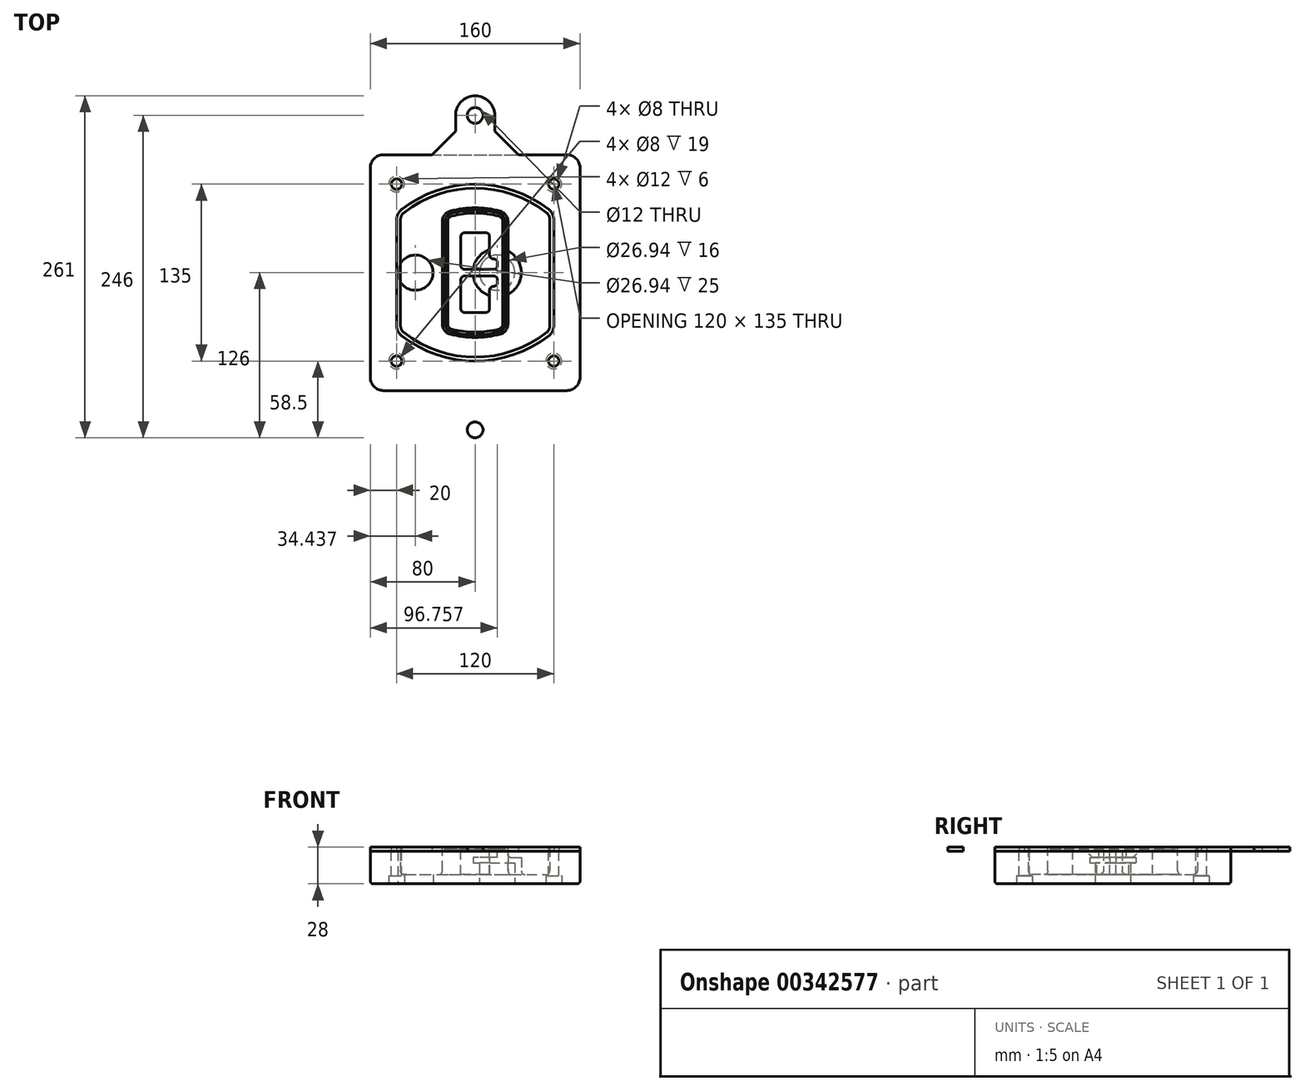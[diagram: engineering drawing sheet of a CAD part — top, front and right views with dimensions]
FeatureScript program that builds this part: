
annotation { "Feature Type Name" : "Feature", "Feature Type Description" : "" }
export const myFeature = defineFeature(function(context is Context, id is Id, definition is map)
    precondition{}
    {
        {
            var Q0;
            Q0=qCreatedBy(makeId("Top.planeOp"),FACE);
            var sketch = newSketch(context, id + "F0", { "sketchPlane" : qUnion([Q0])});
            skPoint(sketch, "E0.rect.middle", {"position": v(0, 0) * mm});
            skLineSegment(sketch, "E1.bottom", {"start": v(-70, -90) * mm, "end": v(70, -90) * mm});
            skLineSegment(sketch, "E1.top", {"start": v(-70, 90) * mm, "end": v(70, 90) * mm});
            skLineSegment(sketch, "E1.left", {"start": v(-80, -80) * mm, "end": v(-80, 80) * mm});
            skLineSegment(sketch, "E1.right", {"start": v(80, -80) * mm, "end": v(80, 80) * mm});
            skLineSegment(sketch, "E2", {"start": v(-80, 90) * mm, "end": v(80, -90) * mm, "construction": true});
            skLineSegment(sketch, "E3", {"start": v(80, 90) * mm, "end": v(-80, -90) * mm, "construction": true});
            skCircle(sketch, "E4", {"center": v(-60, 67.5) * mm, "radius": 4 * mm});
            skCircle(sketch, "E5", {"center": v(60, 67.5) * mm, "radius": 4 * mm});
            skCircle(sketch, "E6", {"center": v(60, -67.5) * mm, "radius": 4 * mm});
            skCircle(sketch, "E7", {"center": v(-60, -67.5) * mm, "radius": 4 * mm});
            skLineSegment(sketch, "E8", {"start": v(-60, 67.5) * mm, "end": v(60, 67.5) * mm, "construction": true});
            skLineSegment(sketch, "E9", {"start": v(60, 67.5) * mm, "end": v(60, -67.5) * mm, "construction": true});
            skLineSegment(sketch, "E10", {"start": v(60, -67.5) * mm, "end": v(-60, -67.5) * mm, "construction": true});
            skLineSegment(sketch, "E11", {"start": v(-60, -67.5) * mm, "end": v(-60, 67.5) * mm, "construction": true});
            skLineSegment(sketch, "E12", {"start": v(-60, 40.3) * mm, "end": v(-60, -40.3) * mm});
            skLineSegment(sketch, "E13", {"start": v(60, 40.3) * mm, "end": v(60, -40.3) * mm});
            skArc(sketch, "E14", {"start": v(56.15, 48.18) * mm, "mid": v(0, 67.5) * mm, "end": v(-56.15, 48.18) * mm});
            skArc(sketch, "E15", {"start": v(-56.15, -48.18) * mm, "mid": v(0, -67.5) * mm, "end": v(56.15, -48.18) * mm});
            skLineSegment(sketch, "E16", {"start": v(-60, 0) * mm, "end": v(60, 0) * mm, "construction": true});
            skPoint(sketch, "E17.visualSharp", {"position": v(-60, -45) * mm});
            skArc(sketch, "E17.filletArc", {"start": v(-60, -40.3) * mm, "mid": v(-58.99, -44.68) * mm, "end": v(-56.15, -48.18) * mm});
            skPoint(sketch, "E18.visualSharp", {"position": v(-60, 45) * mm});
            skArc(sketch, "E18.filletArc", {"start": v(-56.15, 48.18) * mm, "mid": v(-58.99, 44.68) * mm, "end": v(-60, 40.3) * mm});
            skPoint(sketch, "E19.visualSharp", {"position": v(60, 45) * mm});
            skArc(sketch, "E19.filletArc", {"start": v(60, 40.3) * mm, "mid": v(58.99, 44.68) * mm, "end": v(56.15, 48.18) * mm});
            skPoint(sketch, "E20.visualSharp", {"position": v(60, -45) * mm});
            skArc(sketch, "E20.filletArc", {"start": v(56.15, -48.18) * mm, "mid": v(58.99, -44.68) * mm, "end": v(60, -40.3) * mm});
            skPoint(sketch, "E21.visualSharp", {"position": v(-80, 90) * mm});
            skArc(sketch, "E21.filletArc", {"start": v(-70, 90) * mm, "mid": v(-77.07, 87.07) * mm, "end": v(-80, 80) * mm});
            skPoint(sketch, "E22.visualSharp", {"position": v(80, 90) * mm});
            skArc(sketch, "E22.filletArc", {"start": v(80, 80) * mm, "mid": v(77.07, 87.07) * mm, "end": v(70, 90) * mm});
            skPoint(sketch, "E23.visualSharp", {"position": v(80, -90) * mm});
            skArc(sketch, "E23.filletArc", {"start": v(70, -90) * mm, "mid": v(77.07, -87.07) * mm, "end": v(80, -80) * mm});
            skPoint(sketch, "E24.visualSharp", {"position": v(-80, -90) * mm});
            skArc(sketch, "E24.filletArc", {"start": v(-80, -80) * mm, "mid": v(-77.07, -87.07) * mm, "end": v(-70, -90) * mm});
            skArc(sketch, "E25.0", {"start": v(57, 40.3) * mm, "mid": v(56.3, 43.36) * mm, "end": v(54.3, 45.81) * mm});
            skLineSegment(sketch, "E25.1", {"start": v(57, 40.3) * mm, "end": v(57, -40.3) * mm});
            skArc(sketch, "E25.2", {"start": v(54.3, -45.81) * mm, "mid": v(56.3, -43.36) * mm, "end": v(57, -40.3) * mm});
            skArc(sketch, "E25.3", {"start": v(-54.3, -45.81) * mm, "mid": v(0, -64.5) * mm, "end": v(54.3, -45.81) * mm});
            skArc(sketch, "E25.4", {"start": v(-57, -40.3) * mm, "mid": v(-56.3, -43.36) * mm, "end": v(-54.3, -45.81) * mm});
            skArc(sketch, "E25.5", {"start": v(54.3, 45.81) * mm, "mid": v(0, 64.5) * mm, "end": v(-54.3, 45.81) * mm});
            skLineSegment(sketch, "E25.6", {"start": v(-57, 40.3) * mm, "end": v(-57, -40.3) * mm});
            skArc(sketch, "E25.7", {"start": v(-54.3, 45.81) * mm, "mid": v(-56.3, 43.36) * mm, "end": v(-57, 40.3) * mm});
            skArc(sketch, "E26.0", {"start": v(-58.62, 51.33) * mm, "mid": v(-62.58, 46.43) * mm, "end": v(-64, 40.3) * mm});
            skArc(sketch, "E26.1", {"start": v(58.62, 51.33) * mm, "mid": v(0, 71.5) * mm, "end": v(-58.62, 51.33) * mm});
            skArc(sketch, "E26.2", {"start": v(64, 40.3) * mm, "mid": v(62.58, 46.43) * mm, "end": v(58.62, 51.33) * mm});
            skLineSegment(sketch, "E26.3", {"start": v(64, 40.3) * mm, "end": v(64, -40.3) * mm});
            skArc(sketch, "E26.4", {"start": v(58.62, -51.33) * mm, "mid": v(62.58, -46.43) * mm, "end": v(64, -40.3) * mm});
            skLineSegment(sketch, "E26.5", {"start": v(-64, 40.3) * mm, "end": v(-64, -40.3) * mm});
            skArc(sketch, "E26.6", {"start": v(-58.62, -51.33) * mm, "mid": v(0, -71.5) * mm, "end": v(58.62, -51.33) * mm});
            skArc(sketch, "E26.7", {"start": v(-64, -40.3) * mm, "mid": v(-62.58, -46.43) * mm, "end": v(-58.62, -51.33) * mm});
            skSolve(sketch);
        }
        {
            var Q0;
            Q0=makeQuery(id+"F0.imprint","IMPRINT",FACE,{"disambiguationData":[TD([[makeQuery(id+"F0.imprint","IMPRINT",EDGE,{"derivedFrom":sQuery(id+"F0.wireOp",EDGE,"E1.bottom")}),1.0]])]});
            var Q1;
            Q1=makeQuery(id+"F0.imprint","IMPRINT",FACE,{"disambiguationData":[TD([[makeQuery(id+"F0.imprint","IMPRINT",EDGE,{"derivedFrom":sQuery(id+"F0.wireOp",EDGE,"E12")}),1.0]])]});
            var Q2;
            Q2=makeQuery(id+"F0.imprint","IMPRINT",FACE,{"disambiguationData":[TD([[makeQuery(id+"F0.imprint","IMPRINT",EDGE,{"derivedFrom":sQuery(id+"F0.wireOp",EDGE,"E25.0")}),1.0]])]});
            var Q3;
            Q3=makeQuery(id+"F0.imprint","IMPRINT",FACE,{"disambiguationData":[TD([[makeQuery(id+"F0.imprint","IMPRINT",EDGE,{"derivedFrom":sQuery(id+"F0.wireOp",EDGE,"E12")}),-1.0]])]});
            extrude(context, id + "F1", {"entities" : qUnion([Q0, Q1, Q2, Q3]), "oppositeDirection" : true, "depth" : 25 * mm});
        }
        {
            var Q0;
            Q0=makeQuery(id+"F0.imprint","IMPRINT",FACE,{"disambiguationData":[TD([[makeQuery(id+"F0.imprint","IMPRINT",EDGE,{"derivedFrom":sQuery(id+"F0.wireOp",EDGE,"E12")}),1.0]])]});
            extrude(context, id + "F2", {"entities" : qUnion([Q0]), "operationType" : NewBodyOperationType.ADD, "depth" : 3 * mm});
        }
        {
            var Q0;
            Q0=makeQuery(id+"F0.imprint","IMPRINT",FACE,{"disambiguationData":[TD([[makeQuery(id+"F0.imprint","IMPRINT",EDGE,{"derivedFrom":sQuery(id+"F0.wireOp",EDGE,"E25.0")}),1.0]])]});
            extrude(context, id + "F3", {"entities" : qUnion([Q0]), "operationType" : NewBodyOperationType.REMOVE, "oppositeDirection" : true, "depth" : 18 * mm});
        }
        {
            var Q0;
            Q0=makeQuery(id+"F2.opExtrude","CAP_FACE",FACE,{"disambiguationData":[OSD([sQuery(id+"F0.wireOp",EDGE,"E12"),sQuery(id+"F0.wireOp",EDGE,"E13"),sQuery(id+"F0.wireOp",EDGE,"E14"),sQuery(id+"F0.wireOp",EDGE,"E15"),sQuery(id+"F0.wireOp",EDGE,"E17.filletArc"),sQuery(id+"F0.wireOp",EDGE,"E18.filletArc"),sQuery(id+"F0.wireOp",EDGE,"E19.filletArc"),sQuery(id+"F0.wireOp",EDGE,"E20.filletArc"),sQuery(id+"F0.wireOp",EDGE,"E25.0"),sQuery(id+"F0.wireOp",EDGE,"E25.1"),sQuery(id+"F0.wireOp",EDGE,"E25.2"),sQuery(id+"F0.wireOp",EDGE,"E25.3"),sQuery(id+"F0.wireOp",EDGE,"E25.4"),sQuery(id+"F0.wireOp",EDGE,"E25.5"),sQuery(id+"F0.wireOp",EDGE,"E25.6"),sQuery(id+"F0.wireOp",EDGE,"E25.7")])],"isStart":false});
            var sketch = newSketch(context, id + "F4", { "sketchPlane" : qUnion([Q0])});
            skArc(sketch, "E27.0", {"start": v(-19.08, -46.97) * mm, "mid": v(0, -49.5) * mm, "end": v(19.08, -46.97) * mm});
            skArc(sketch, "E28.0", {"start": v(19.08, 46.97) * mm, "mid": v(0, 49.5) * mm, "end": v(-19.08, 46.97) * mm});
            skLineSegment(sketch, "E29", {"start": v(-25, 39.25) * mm, "end": v(-25, -39.25) * mm});
            skLineSegment(sketch, "E30", {"start": v(25, 39.25) * mm, "end": v(25, -39.25) * mm});
            skLineSegment(sketch, "E31", {"start": v(-25, 45.1) * mm, "end": v(25, 45.1) * mm, "construction": true});
            skLineSegment(sketch, "E32", {"start": v(-25, -45.1) * mm, "end": v(25, -45.1) * mm, "construction": true});
            skPoint(sketch, "E33.visualSharp", {"position": v(-25, 45.1) * mm});
            skArc(sketch, "E33.filletArc", {"start": v(-19.08, 46.97) * mm, "mid": v(-23.35, 44.11) * mm, "end": v(-25, 39.25) * mm});
            skPoint(sketch, "E34.visualSharp", {"position": v(25, 45.1) * mm});
            skArc(sketch, "E34.filletArc", {"start": v(25, 39.25) * mm, "mid": v(23.35, 44.11) * mm, "end": v(19.08, 46.97) * mm});
            skPoint(sketch, "E35.visualSharp", {"position": v(25, -45.1) * mm});
            skArc(sketch, "E35.filletArc", {"start": v(19.08, -46.97) * mm, "mid": v(23.35, -44.11) * mm, "end": v(25, -39.25) * mm});
            skPoint(sketch, "E36.visualSharp", {"position": v(-25, -45.1) * mm});
            skArc(sketch, "E36.filletArc", {"start": v(-25, -39.25) * mm, "mid": v(-23.35, -44.11) * mm, "end": v(-19.08, -46.97) * mm});
            skArc(sketch, "E37.0", {"start": v(54.3, 45.81) * mm, "mid": v(0, 64.5) * mm, "end": v(-54.3, 45.81) * mm});
            skArc(sketch, "E37.1", {"start": v(-54.3, 45.81) * mm, "mid": v(-56.3, 43.36) * mm, "end": v(-57, 40.3) * mm});
            skLineSegment(sketch, "E37.2", {"start": v(-57, 40.3) * mm, "end": v(-57, -40.3) * mm});
            skArc(sketch, "E37.3", {"start": v(-57, -40.3) * mm, "mid": v(-56.3, -43.36) * mm, "end": v(-54.3, -45.81) * mm});
            skArc(sketch, "E37.4", {"start": v(-54.3, -45.81) * mm, "mid": v(0, -64.5) * mm, "end": v(54.3, -45.81) * mm});
            skArc(sketch, "E37.5", {"start": v(54.3, -45.81) * mm, "mid": v(56.3, -43.36) * mm, "end": v(57, -40.3) * mm});
            skLineSegment(sketch, "E37.6", {"start": v(57, 40.3) * mm, "end": v(57, -40.3) * mm});
            skArc(sketch, "E37.7", {"start": v(57, 40.3) * mm, "mid": v(56.3, 43.36) * mm, "end": v(54.3, 45.81) * mm});
            skLineSegment(sketch, "E38.0", {"start": v(23, 39.25) * mm, "end": v(23, -39.25) * mm});
            skArc(sketch, "E38.1", {"start": v(18.56, -45.04) * mm, "mid": v(21.76, -42.9) * mm, "end": v(23, -39.25) * mm});
            skArc(sketch, "E38.2", {"start": v(-18.56, -45.04) * mm, "mid": v(0, -47.5) * mm, "end": v(18.56, -45.04) * mm});
            skArc(sketch, "E38.3", {"start": v(-23, -39.25) * mm, "mid": v(-21.76, -42.9) * mm, "end": v(-18.56, -45.04) * mm});
            skLineSegment(sketch, "E38.4", {"start": v(-23, 39.25) * mm, "end": v(-23, -39.25) * mm});
            skArc(sketch, "E38.5", {"start": v(23, 39.25) * mm, "mid": v(21.76, 42.9) * mm, "end": v(18.56, 45.04) * mm});
            skArc(sketch, "E38.6", {"start": v(-18.56, 45.04) * mm, "mid": v(-21.76, 42.9) * mm, "end": v(-23, 39.25) * mm});
            skArc(sketch, "E38.7", {"start": v(18.56, 45.04) * mm, "mid": v(0, 47.5) * mm, "end": v(-18.56, 45.04) * mm});
            skArc(sketch, "E39.0", {"start": v(21, 39.25) * mm, "mid": v(20.18, 41.68) * mm, "end": v(18.04, 43.1) * mm});
            skLineSegment(sketch, "E39.1", {"start": v(21, 39.25) * mm, "end": v(21, -39.25) * mm});
            skArc(sketch, "E39.2", {"start": v(18.04, -43.1) * mm, "mid": v(20.18, -41.68) * mm, "end": v(21, -39.25) * mm});
            skArc(sketch, "E39.3", {"start": v(-18.04, -43.1) * mm, "mid": v(0, -45.5) * mm, "end": v(18.04, -43.1) * mm});
            skArc(sketch, "E39.4", {"start": v(-21, -39.25) * mm, "mid": v(-20.18, -41.68) * mm, "end": v(-18.04, -43.1) * mm});
            skArc(sketch, "E39.5", {"start": v(18.04, 43.1) * mm, "mid": v(0, 45.5) * mm, "end": v(-18.04, 43.1) * mm});
            skLineSegment(sketch, "E39.6", {"start": v(-21, 39.25) * mm, "end": v(-21, -39.25) * mm});
            skArc(sketch, "E39.7", {"start": v(-18.04, 43.1) * mm, "mid": v(-20.18, 41.68) * mm, "end": v(-21, 39.25) * mm});
            skLineSegment(sketch, "E40", {"start": v(-25, 0) * mm, "end": v(25, 0) * mm, "construction": true});
            skLineSegment(sketch, "E41", {"start": v(-11, 5.5) * mm, "end": v(-11, 27.5) * mm});
            skLineSegment(sketch, "E42", {"start": v(-8, 30.5) * mm, "end": v(8, 30.5) * mm});
            skLineSegment(sketch, "E43", {"start": v(11, 27.5) * mm, "end": v(11, 13.5) * mm});
            skLineSegment(sketch, "E44", {"start": v(14, 10.5) * mm, "end": v(14, 10.5) * mm});
            skLineSegment(sketch, "E45", {"start": v(17, 7.5) * mm, "end": v(17, 5.5) * mm});
            skLineSegment(sketch, "E46", {"start": v(14, 2.5) * mm, "end": v(-8, 2.5) * mm});
            skPoint(sketch, "E47.visualSharp", {"position": v(-11, 30.5) * mm});
            skArc(sketch, "E47.filletArc", {"start": v(-8, 30.5) * mm, "mid": v(-10.12, 29.62) * mm, "end": v(-11, 27.5) * mm});
            skPoint(sketch, "E48.visualSharp", {"position": v(11, 30.5) * mm});
            skArc(sketch, "E48.filletArc", {"start": v(11, 27.5) * mm, "mid": v(10.12, 29.62) * mm, "end": v(8, 30.5) * mm});
            skPoint(sketch, "E49.visualSharp", {"position": v(11, 10.5) * mm});
            skArc(sketch, "E49.filletArc", {"start": v(11, 13.5) * mm, "mid": v(11.88, 11.38) * mm, "end": v(14, 10.5) * mm});
            skPoint(sketch, "E50.visualSharp", {"position": v(17, 10.5) * mm});
            skArc(sketch, "E50.filletArc", {"start": v(17, 7.5) * mm, "mid": v(16.12, 9.62) * mm, "end": v(14, 10.5) * mm});
            skPoint(sketch, "E51.visualSharp", {"position": v(17, 2.5) * mm});
            skArc(sketch, "E51.filletArc", {"start": v(14, 2.5) * mm, "mid": v(16.12, 3.38) * mm, "end": v(17, 5.5) * mm});
            skPoint(sketch, "E52.visualSharp", {"position": v(-11, 2.5) * mm});
            skArc(sketch, "E52.filletArc", {"start": v(-11, 5.5) * mm, "mid": v(-10.12, 3.38) * mm, "end": v(-8, 2.5) * mm});
            skLineSegment(sketch, "E53.0.MirrorCS", {"start": v(14, -2.5) * mm, "end": v(-8, -2.5) * mm});
            skArc(sketch, "E54.0.MirrorCS", {"start": v(-11, -5.5) * mm, "mid": v(-10.12, -3.38) * mm, "end": v(-8, -2.5) * mm});
            skLineSegment(sketch, "E55.0.MirrorCS", {"start": v(-11, -5.5) * mm, "end": v(-11, -27.5) * mm});
            skArc(sketch, "E56.0.MirrorCS", {"start": v(-8, -30.5) * mm, "mid": v(-10.12, -29.62) * mm, "end": v(-11, -27.5) * mm});
            skLineSegment(sketch, "E57.0.MirrorCS", {"start": v(-8, -30.5) * mm, "end": v(8, -30.5) * mm});
            skArc(sketch, "E58.0.MirrorCS", {"start": v(11, -27.5) * mm, "mid": v(10.12, -29.62) * mm, "end": v(8, -30.5) * mm});
            skLineSegment(sketch, "E59.0.MirrorCS", {"start": v(11, -27.5) * mm, "end": v(11, -13.5) * mm});
            skArc(sketch, "E60.0.MirrorCS", {"start": v(11, -13.5) * mm, "mid": v(11.88, -11.38) * mm, "end": v(14, -10.5) * mm});
            skArc(sketch, "E61.0.MirrorCS", {"start": v(17, -7.5) * mm, "mid": v(16.12, -9.62) * mm, "end": v(14, -10.5) * mm});
            skLineSegment(sketch, "E62.0.MirrorCS", {"start": v(17, -7.5) * mm, "end": v(17, -5.5) * mm});
            skArc(sketch, "E63.0.MirrorCS", {"start": v(14, -2.5) * mm, "mid": v(16.12, -3.38) * mm, "end": v(17, -5.5) * mm});
            skSolve(sketch);
        }
        {
            var Q0;
            Q0=makeQuery(id+"F4.imprint","IMPRINT",FACE,{"disambiguationData":[TD([[makeQuery(id+"F4.imprint","IMPRINT",EDGE,{"derivedFrom":sQuery(id+"F4.wireOp",EDGE,"E27.0")}),1.0]])]});
            var Q1;
            Q1=makeQuery(id+"F4.imprint","IMPRINT",FACE,{"disambiguationData":[TD([[makeQuery(id+"F4.imprint","IMPRINT",EDGE,{"derivedFrom":sQuery(id+"F4.wireOp",EDGE,"E38.0")}),-1.0]])]});
            var Q2;
            Q2=makeQuery(id+"F4.imprint","IMPRINT",FACE,{"disambiguationData":[TD([[makeQuery(id+"F4.imprint","IMPRINT",EDGE,{"derivedFrom":sQuery(id+"F4.wireOp",EDGE,"E39.0")}),1.0]])]});
            extrude(context, id + "F5", {"entities" : qUnion([Q0, Q1, Q2]), "operationType" : NewBodyOperationType.ADD, "endBound" : BoundingType.UP_TO_NEXT, "oppositeDirection" : true, "depth" : 25 * mm});
        }
        {
            var Q0;
            Q0=makeQuery(id+"F4.imprint","IMPRINT",FACE,{"disambiguationData":[TD([[makeQuery(id+"F4.imprint","IMPRINT",EDGE,{"derivedFrom":sQuery(id+"F4.wireOp",EDGE,"E38.0")}),-1.0]])]});
            extrude(context, id + "F6", {"entities" : qUnion([Q0]), "operationType" : NewBodyOperationType.REMOVE, "oppositeDirection" : true, "depth" : 2 * mm});
        }
        {
            var Q0;
            Q0=makeQuery(id+"F1.opExtrude","CAP_FACE",FACE,{"disambiguationData":[OSD([sQuery(id+"F0.wireOp",EDGE,"E1.bottom"),sQuery(id+"F0.wireOp",EDGE,"E1.top"),sQuery(id+"F0.wireOp",EDGE,"E1.left"),sQuery(id+"F0.wireOp",EDGE,"E1.right"),sQuery(id+"F0.wireOp",EDGE,"E4"),sQuery(id+"F0.wireOp",EDGE,"E5"),sQuery(id+"F0.wireOp",EDGE,"E6"),sQuery(id+"F0.wireOp",EDGE,"E7"),sQuery(id+"F0.wireOp",EDGE,"E21.filletArc"),sQuery(id+"F0.wireOp",EDGE,"E22.filletArc"),sQuery(id+"F0.wireOp",EDGE,"E23.filletArc"),sQuery(id+"F0.wireOp",EDGE,"E24.filletArc")])],"isStart":false});
            var sketch = newSketch(context, id + "F7", { "sketchPlane" : qUnion([Q0])});
            skCircle(sketch, "E64", {"center": v(16.76, 0) * mm, "radius": 13.47 * mm});
            skCircle(sketch, "E65", {"center": v(-45.56, 0) * mm, "radius": 13.47 * mm});
            skLineSegment(sketch, "E66", {"start": v(80, 0) * mm, "end": v(-80, 0) * mm});
            skCircle(sketch, "E67", {"center": v(16.76, 0) * mm, "radius": 18.47 * mm});
            skCircle(sketch, "E68", {"center": v(60, -67.5) * mm, "radius": 6 * mm});
            skCircle(sketch, "E69", {"center": v(-60, -67.5) * mm, "radius": 6 * mm});
            skCircle(sketch, "E70", {"center": v(-60, 67.5) * mm, "radius": 6 * mm});
            skCircle(sketch, "E71", {"center": v(60, 67.5) * mm, "radius": 6 * mm});
            skSolve(sketch);
        }
        {
            var Q0;
            {var subQ1=sQuery(id+"F7.wireOp",EDGE,"E66");var subQ4=sQuery(id+"F7.wireOp",EDGE,"E64");var subQ6=makeQuery(id+"F7.imprint","INTERSECT",VERTEX,{"disambiguationData":[OD(0.0)],"derivedFrom":[subQ4,subQ1]});Q0=makeQuery(id+"F7.imprint","IMPRINT",FACE,{"disambiguationData":[TD([[makeQuery(id+"F7.imprint","IMPRINT",EDGE,{"disambiguationData":[TD([[subQ6,-1.0]])],"derivedFrom":subQ4}),-1.0]])]});}
            var Q1;
            {var subQ0=sQuery(id+"F7.wireOp",EDGE,"E66");var subQ1=sQuery(id+"F7.wireOp",EDGE,"E64");var subQ3=makeQuery(id+"F7.imprint","INTERSECT",VERTEX,{"disambiguationData":[OD(0.0)],"derivedFrom":[subQ1,subQ0]});Q1=makeQuery(id+"F7.imprint","IMPRINT",FACE,{"disambiguationData":[TD([[makeQuery(id+"F7.imprint","IMPRINT",EDGE,{"disambiguationData":[TD([[subQ3,-1.0]])],"derivedFrom":subQ1}),1.0]])]});}
            var Q2;
            {var subQ0=sQuery(id+"F7.wireOp",EDGE,"E66");var subQ1=sQuery(id+"F7.wireOp",EDGE,"E64");var subQ3=makeQuery(id+"F7.imprint","INTERSECT",VERTEX,{"disambiguationData":[OD(0.0)],"derivedFrom":[subQ1,subQ0]});Q2=makeQuery(id+"F7.imprint","IMPRINT",FACE,{"disambiguationData":[TD([[makeQuery(id+"F7.imprint","IMPRINT",EDGE,{"disambiguationData":[TD([[subQ3,1.0]])],"derivedFrom":subQ1}),1.0]])]});}
            var Q3;
            {var subQ1=sQuery(id+"F7.wireOp",EDGE,"E66");var subQ4=sQuery(id+"F7.wireOp",EDGE,"E64");var subQ6=makeQuery(id+"F7.imprint","INTERSECT",VERTEX,{"disambiguationData":[OD(0.0)],"derivedFrom":[subQ4,subQ1]});Q3=makeQuery(id+"F7.imprint","IMPRINT",FACE,{"disambiguationData":[TD([[makeQuery(id+"F7.imprint","IMPRINT",EDGE,{"disambiguationData":[TD([[subQ6,1.0]])],"derivedFrom":subQ4}),-1.0]])]});}
            extrude(context, id + "F8", {"entities" : qUnion([Q0, Q1, Q2, Q3]), "operationType" : NewBodyOperationType.ADD, "oppositeDirection" : true, "depth" : 20 * mm});
        }
        {
            var Q0;
            {var subQ0=sQuery(id+"F7.wireOp",EDGE,"E66");var subQ1=sQuery(id+"F7.wireOp",EDGE,"E64");var subQ3=makeQuery(id+"F7.imprint","INTERSECT",VERTEX,{"disambiguationData":[OD(0.0)],"derivedFrom":[subQ1,subQ0]});Q0=makeQuery(id+"F7.imprint","IMPRINT",FACE,{"disambiguationData":[TD([[makeQuery(id+"F7.imprint","IMPRINT",EDGE,{"disambiguationData":[TD([[subQ3,-1.0]])],"derivedFrom":subQ1}),1.0]])]});}
            var Q1;
            {var subQ0=sQuery(id+"F7.wireOp",EDGE,"E66");var subQ1=sQuery(id+"F7.wireOp",EDGE,"E64");var subQ3=makeQuery(id+"F7.imprint","INTERSECT",VERTEX,{"disambiguationData":[OD(0.0)],"derivedFrom":[subQ1,subQ0]});Q1=makeQuery(id+"F7.imprint","IMPRINT",FACE,{"disambiguationData":[TD([[makeQuery(id+"F7.imprint","IMPRINT",EDGE,{"disambiguationData":[TD([[subQ3,1.0]])],"derivedFrom":subQ1}),1.0]])]});}
            extrude(context, id + "F9", {"entities" : qUnion([Q0, Q1]), "operationType" : NewBodyOperationType.REMOVE, "oppositeDirection" : true, "depth" : 16 * mm});
        }
        {
            var Q0;
            {var subQ0=sQuery(id+"F7.wireOp",EDGE,"E66");var subQ1=sQuery(id+"F7.wireOp",EDGE,"E65");var subQ3=makeQuery(id+"F7.imprint","INTERSECT",VERTEX,{"disambiguationData":[OD(0.0)],"derivedFrom":[subQ1,subQ0]});Q0=makeQuery(id+"F7.imprint","IMPRINT",FACE,{"disambiguationData":[TD([[makeQuery(id+"F7.imprint","IMPRINT",EDGE,{"disambiguationData":[TD([[subQ3,-1.0]])],"derivedFrom":subQ1}),1.0]])]});}
            var Q1;
            {var subQ0=sQuery(id+"F7.wireOp",EDGE,"E66");var subQ1=sQuery(id+"F7.wireOp",EDGE,"E65");var subQ3=makeQuery(id+"F7.imprint","INTERSECT",VERTEX,{"disambiguationData":[OD(0.0)],"derivedFrom":[subQ1,subQ0]});Q1=makeQuery(id+"F7.imprint","IMPRINT",FACE,{"disambiguationData":[TD([[makeQuery(id+"F7.imprint","IMPRINT",EDGE,{"disambiguationData":[TD([[subQ3,1.0]])],"derivedFrom":subQ1}),1.0]])]});}
            extrude(context, id + "F10", {"entities" : qUnion([Q0, Q1]), "operationType" : NewBodyOperationType.REMOVE, "oppositeDirection" : true, "depth" : 25 * mm});
        }
        {
            var Q0;
            Q0=makeQuery(id+"F7.imprint","IMPRINT",FACE,{"disambiguationData":[TD([[makeQuery(id+"F7.imprint","IMPRINT",EDGE,{"derivedFrom":sQuery(id+"F7.wireOp",EDGE,"E68")}),1.0]])]});
            var Q1;
            Q1=makeQuery(id+"F7.imprint","IMPRINT",FACE,{"disambiguationData":[TD([[makeQuery(id+"F7.imprint","IMPRINT",EDGE,{"derivedFrom":makeQuery(id+"F1.opExtrude","CAP_EDGE",EDGE,{"disambiguationData":[OSD([sQuery(id+"F0.wireOp",EDGE,"E5")])],"isStart":false})}),-1.0]])]});
            var Q2;
            Q2=makeQuery(id+"F7.imprint","IMPRINT",FACE,{"disambiguationData":[TD([[makeQuery(id+"F7.imprint","IMPRINT",EDGE,{"derivedFrom":sQuery(id+"F7.wireOp",EDGE,"E69")}),1.0]])]});
            var Q3;
            Q3=makeQuery(id+"F7.imprint","IMPRINT",FACE,{"disambiguationData":[TD([[makeQuery(id+"F7.imprint","IMPRINT",EDGE,{"derivedFrom":makeQuery(id+"F1.opExtrude","CAP_EDGE",EDGE,{"disambiguationData":[OSD([sQuery(id+"F0.wireOp",EDGE,"E4")])],"isStart":false})}),-1.0]])]});
            var Q4;
            Q4=makeQuery(id+"F7.imprint","IMPRINT",FACE,{"disambiguationData":[TD([[makeQuery(id+"F7.imprint","IMPRINT",EDGE,{"derivedFrom":sQuery(id+"F7.wireOp",EDGE,"E70")}),1.0]])]});
            var Q5;
            Q5=makeQuery(id+"F7.imprint","IMPRINT",FACE,{"disambiguationData":[TD([[makeQuery(id+"F7.imprint","IMPRINT",EDGE,{"derivedFrom":makeQuery(id+"F1.opExtrude","CAP_EDGE",EDGE,{"disambiguationData":[OSD([sQuery(id+"F0.wireOp",EDGE,"E7")])],"isStart":false})}),-1.0]])]});
            var Q6;
            Q6=makeQuery(id+"F7.imprint","IMPRINT",FACE,{"disambiguationData":[TD([[makeQuery(id+"F7.imprint","IMPRINT",EDGE,{"derivedFrom":sQuery(id+"F7.wireOp",EDGE,"E71")}),1.0]])]});
            var Q7;
            Q7=makeQuery(id+"F7.imprint","IMPRINT",FACE,{"disambiguationData":[TD([[makeQuery(id+"F7.imprint","IMPRINT",EDGE,{"derivedFrom":makeQuery(id+"F1.opExtrude","CAP_EDGE",EDGE,{"disambiguationData":[OSD([sQuery(id+"F0.wireOp",EDGE,"E6")])],"isStart":false})}),-1.0]])]});
            extrude(context, id + "F11", {"entities" : qUnion([Q0, Q1, Q2, Q3, Q4, Q5, Q6, Q7]), "operationType" : NewBodyOperationType.REMOVE, "oppositeDirection" : true, "depth" : 6 * mm});
        }
        {
            var Q0;
            Q0=makeQuery(id+"F9.boolean.opBoolean","COPY",FACE,{"derivedFrom":makeQuery(id+"F9.opExtrude","CAP_FACE",FACE,{"disambiguationData":[OSD([sQuery(id+"F7.wireOp",EDGE,"E64")])],"isStart":false})});
            var sketch = newSketch(context, id + "F12", { "sketchPlane" : qUnion([Q0])});
            skArc(sketch, "E72.0", {"start": v(11, 17.55) * mm, "mid": v(2.57, 11.82) * mm, "end": v(-1.54, 2.5) * mm});
            skArc(sketch, "E72.1", {"start": v(-1.54, -2.5) * mm, "mid": v(2.57, -11.82) * mm, "end": v(11, -17.55) * mm});
            skLineSegment(sketch, "E73", {"start": v(-1.54, -2.5) * mm, "end": v(14, -2.5) * mm});
            skLineSegment(sketch, "E74.0", {"start": v(14, 2.5) * mm, "end": v(-1.54, 2.5) * mm});
            skArc(sketch, "E74.1", {"start": v(14, 2.5) * mm, "mid": v(16.12, 3.38) * mm, "end": v(17, 5.5) * mm});
            skLineSegment(sketch, "E74.2", {"start": v(17, 7.5) * mm, "end": v(17, 5.5) * mm});
            skArc(sketch, "E74.3", {"start": v(17, 7.5) * mm, "mid": v(16.12, 9.62) * mm, "end": v(14, 10.5) * mm});
            skArc(sketch, "E74.4", {"start": v(11, 13.5) * mm, "mid": v(11.88, 11.38) * mm, "end": v(14, 10.5) * mm});
            skLineSegment(sketch, "E74.5", {"start": v(11, 17.55) * mm, "end": v(11, 13.5) * mm});
            skLineSegment(sketch, "E74.7", {"start": v(14, -2.5) * mm, "end": v(-1.54, -2.5) * mm});
            skArc(sketch, "E74.8", {"start": v(14, -2.5) * mm, "mid": v(16.12, -3.38) * mm, "end": v(17, -5.5) * mm});
            skLineSegment(sketch, "E74.9", {"start": v(17, -7.5) * mm, "end": v(17, -5.5) * mm});
            skArc(sketch, "E74.10", {"start": v(17, -7.5) * mm, "mid": v(16.12, -9.62) * mm, "end": v(14, -10.5) * mm});
            skArc(sketch, "E74.11", {"start": v(11, -13.5) * mm, "mid": v(11.88, -11.38) * mm, "end": v(14, -10.5) * mm});
            skLineSegment(sketch, "E74.12", {"start": v(11, -17.55) * mm, "end": v(11, -13.5) * mm});
            skPoint(sketch, "E75.orphan", {"position": v(11, -27.5) * mm});
            skPoint(sketch, "E76.orphan", {"position": v(-8, -2.5) * mm});
            skPoint(sketch, "E77.orphan", {"position": v(-8, 2.5) * mm});
            skPoint(sketch, "E78.orphan", {"position": v(11, 27.5) * mm});
            skSolve(sketch);
        }
        {
            var Q0;
            {var subQ7=sQuery(id+"F12.wireOp",EDGE,"E72.0");var subQ14=sQuery(id+"F12.wireOp",EDGE,"E72.1");var subQ16=sQuery(id+"F12.wireOp",EDGE,"E74.1");var subQ18=sQuery(id+"F12.wireOp",EDGE,"E74.8");Q0=qUnion([makeQuery(id+"F12.imprint","IMPRINT",FACE,{"disambiguationData":[TD([[makeQuery(id+"F12.imprint","IMPRINT",EDGE,{"derivedFrom":subQ7}),1.0]])]}),makeQuery(id+"F12.imprint","IMPRINT",FACE,{"disambiguationData":[TD([[makeQuery(id+"F12.imprint","IMPRINT",EDGE,{"derivedFrom":subQ14}),1.0]])]}),makeQuery(id+"F12.imprint","IMPRINT",FACE,{"disambiguationData":[TD([[makeQuery(id+"F12.imprint","IMPRINT",EDGE,{"derivedFrom":subQ16}),1.0]])]}),makeQuery(id+"F12.imprint","IMPRINT",FACE,{"disambiguationData":[TD([[makeQuery(id+"F12.imprint","IMPRINT",EDGE,{"derivedFrom":subQ18}),-1.0]])]})]);}
            var Q1;
            Q1=makeQuery(id+"F5.boolean.opBoolean","SPLIT",FACE,{"disambiguationData":[TD([makeQuery(id+"F5.opExtrude","SWEPT_FACE",FACE,{"disambiguationData":[OSD([sQuery(id+"F4.wireOp",EDGE,"E41")])]})])],"derivedFrom":makeQuery(id+"F3.boolean.opBoolean","COPY",FACE,{"derivedFrom":makeQuery(id+"F3.opExtrude","CAP_FACE",FACE,{"disambiguationData":[OSD([sQuery(id+"F0.wireOp",EDGE,"E25.0"),sQuery(id+"F0.wireOp",EDGE,"E25.1"),sQuery(id+"F0.wireOp",EDGE,"E25.2"),sQuery(id+"F0.wireOp",EDGE,"E25.3"),sQuery(id+"F0.wireOp",EDGE,"E25.4"),sQuery(id+"F0.wireOp",EDGE,"E25.5"),sQuery(id+"F0.wireOp",EDGE,"E25.6"),sQuery(id+"F0.wireOp",EDGE,"E25.7")])],"isStart":false})})});
            extrude(context, id + "F13", {"entities" : qUnion([Q0]), "operationType" : NewBodyOperationType.REMOVE, "endBound" : BoundingType.UP_TO_SURFACE, "endBoundEntityFace" : qUnion([Q1]), "depth" : 25 * mm});
        }
        {
            var Q0;
            Q0=makeQuery(id+"F3.boolean.opBoolean","COPY",EDGE,{"derivedFrom":makeQuery(id+"F3.opExtrude","CAP_EDGE",EDGE,{"disambiguationData":[OSD([sQuery(id+"F0.wireOp",EDGE,"E25.6")])],"isStart":false})});
            var Q1;
            Q1=makeQuery(id+"F8.boolean.opBoolean","INTERSECT",EDGE,{"derivedFrom":[makeQuery(id+"F5.opExtrude","SWEPT_FACE",FACE,{"disambiguationData":[OSD([sQuery(id+"F4.wireOp",EDGE,"E30")])]}),makeQuery(id+"F8.opExtrude","CAP_FACE",FACE,{"disambiguationData":[OSD([sQuery(id+"F7.wireOp",EDGE,"E67")])],"isStart":false})]});
            var Q2;
            Q2=makeQuery(id+"F8.boolean.opBoolean","INTERSECT",EDGE,{"disambiguationData":[OD(1.0)],"derivedFrom":[makeQuery(id+"F5.opExtrude","SWEPT_FACE",FACE,{"disambiguationData":[OSD([sQuery(id+"F4.wireOp",EDGE,"E30")])]}),makeQuery(id+"F8.opExtrude","SWEPT_FACE",FACE,{"disambiguationData":[OSD([sQuery(id+"F7.wireOp",EDGE,"E67")])]})]});
            var Q3;
            {var subQ0=sQuery(id+"F4.wireOp",EDGE,"E30");Q3=makeQuery(id+"F8.boolean.opBoolean","SPLIT",EDGE,{"disambiguationData":[TD([makeQuery(id+"F5.opExtrude","SWEPT_FACE",FACE,{"disambiguationData":[OSD([sQuery(id+"F4.wireOp",EDGE,"E35.filletArc")])]})])],"derivedFrom":makeQuery(id+"F5.opExtrude","CAP_EDGE",EDGE,{"disambiguationData":[OSD([subQ0])],"isStart":false})});}
            var Q4;
            {var subQ0=sQuery(id+"F0.wireOp",EDGE,"E25.7");var subQ1=sQuery(id+"F0.wireOp",EDGE,"E25.1");var subQ2=sQuery(id+"F0.wireOp",EDGE,"E25.6");var subQ3=sQuery(id+"F0.wireOp",EDGE,"E25.5");var subQ4=sQuery(id+"F0.wireOp",EDGE,"E25.4");var subQ5=sQuery(id+"F0.wireOp",EDGE,"E25.0");var subQ6=sQuery(id+"F0.wireOp",EDGE,"E25.2");var subQ7=sQuery(id+"F0.wireOp",EDGE,"E25.3");Q4=makeQuery(id+"F8.boolean.opBoolean","INTERSECT",EDGE,{"derivedFrom":[makeQuery(id+"F5.boolean.opBoolean","SPLIT",FACE,{"disambiguationData":[TD([makeQuery(id+"F2.opExtrude","SWEPT_FACE",FACE,{"disambiguationData":[OSD([subQ5])]})])],"derivedFrom":makeQuery(id+"F3.boolean.opBoolean","COPY",FACE,{"derivedFrom":makeQuery(id+"F3.opExtrude","CAP_FACE",FACE,{"disambiguationData":[OSD([subQ5,subQ1,subQ6,subQ7,subQ4,subQ3,subQ2,subQ0])],"isStart":false})})}),makeQuery(id+"F8.opExtrude","SWEPT_FACE",FACE,{"disambiguationData":[OSD([sQuery(id+"F7.wireOp",EDGE,"E67")])]})]});}
            var Q5;
            Q5=makeQuery(id+"F8.boolean.opBoolean","INTERSECT",EDGE,{"disambiguationData":[OD(0.0)],"derivedFrom":[makeQuery(id+"F5.opExtrude","SWEPT_FACE",FACE,{"disambiguationData":[OSD([sQuery(id+"F4.wireOp",EDGE,"E30")])]}),makeQuery(id+"F8.opExtrude","SWEPT_FACE",FACE,{"disambiguationData":[OSD([sQuery(id+"F7.wireOp",EDGE,"E67")])]})]});
            fillet(context, id + "F14", {"entities" : qUnion([Q0, Q1, Q2, Q3, Q4, Q5]), "radius" : 3 * mm, "tangentPropagation" : true, "allowEdgeOverflow" : false});
        }
        {
            var Q0;
            Q0=makeQuery(id+"F1.opExtrude","CAP_EDGE",EDGE,{"disambiguationData":[OSD([sQuery(id+"F0.wireOp",EDGE,"E1.bottom")])],"isStart":false});
            fillet(context, id + "F15", {"entities" : qUnion([Q0]), "radius" : 2 * mm, "tangentPropagation" : true, "allowEdgeOverflow" : false});
        }
        {
            var Q0;
            {var subQ0=sQuery(id+"F0.wireOp",EDGE,"E21.filletArc");var subQ1=sQuery(id+"F0.wireOp",EDGE,"E7");var subQ2=sQuery(id+"F0.wireOp",EDGE,"E6");var subQ3=sQuery(id+"F0.wireOp",EDGE,"E5");var subQ4=sQuery(id+"F0.wireOp",EDGE,"E4");var subQ5=sQuery(id+"F0.wireOp",EDGE,"E22.filletArc");var subQ6=sQuery(id+"F0.wireOp",EDGE,"E1.bottom");var subQ7=sQuery(id+"F0.wireOp",EDGE,"E1.right");var subQ8=sQuery(id+"F0.wireOp",EDGE,"E1.top");var subQ9=sQuery(id+"F0.wireOp",EDGE,"E1.left");var subQ10=sQuery(id+"F0.wireOp",EDGE,"E23.filletArc");var subQ11=sQuery(id+"F0.wireOp",EDGE,"E24.filletArc");Q0=makeQuery(id+"F2.boolean.opBoolean","SPLIT",FACE,{"disambiguationData":[TD([makeQuery(id+"F1.opExtrude","SWEPT_FACE",FACE,{"disambiguationData":[OSD([subQ6])]})])],"derivedFrom":makeQuery(id+"F1.opExtrude","CAP_FACE",FACE,{"disambiguationData":[OSD([subQ6,subQ8,subQ9,subQ7,subQ4,subQ3,subQ2,subQ1,subQ0,subQ5,subQ10,subQ11])],"isStart":true})});}
            var sketch = newSketch(context, id + "F16", { "sketchPlane" : qUnion([Q0])});
            skLineSegment(sketch, "E79.0", {"start": v(-70, 90) * mm, "end": v(70, 90) * mm});
            skArc(sketch, "E80.0", {"start": v(80, 80) * mm, "mid": v(77.07, 87.07) * mm, "end": v(70, 90) * mm});
            skLineSegment(sketch, "E81.0", {"start": v(80, -80) * mm, "end": v(80, 80) * mm});
            skArc(sketch, "E82.0", {"start": v(70, -90) * mm, "mid": v(77.07, -87.07) * mm, "end": v(80, -80) * mm});
            skLineSegment(sketch, "E83.0", {"start": v(-70, -90) * mm, "end": v(70, -90) * mm});
            skArc(sketch, "E84.0", {"start": v(-80, -80) * mm, "mid": v(-77.07, -87.07) * mm, "end": v(-70, -90) * mm});
            skLineSegment(sketch, "E85.0", {"start": v(-80, -80) * mm, "end": v(-80, 80) * mm});
            skArc(sketch, "E86.0", {"start": v(-70, 90) * mm, "mid": v(-77.07, 87.07) * mm, "end": v(-80, 80) * mm});
            skArc(sketch, "E87.0", {"start": v(56.15, 48.18) * mm, "mid": v(0, 67.5) * mm, "end": v(-56.15, 48.18) * mm});
            skArc(sketch, "E88.0", {"start": v(60, 40.3) * mm, "mid": v(58.99, 44.68) * mm, "end": v(56.15, 48.18) * mm});
            skLineSegment(sketch, "E89.0", {"start": v(60, 40.3) * mm, "end": v(60, -40.3) * mm});
            skArc(sketch, "E90.0", {"start": v(56.15, -48.18) * mm, "mid": v(58.99, -44.68) * mm, "end": v(60, -40.3) * mm});
            skArc(sketch, "E91.0", {"start": v(-56.15, -48.18) * mm, "mid": v(0, -67.5) * mm, "end": v(56.15, -48.18) * mm});
            skArc(sketch, "E92.0", {"start": v(-60, -40.3) * mm, "mid": v(-58.99, -44.68) * mm, "end": v(-56.15, -48.18) * mm});
            skLineSegment(sketch, "E93.0", {"start": v(-60, 40.3) * mm, "end": v(-60, -40.3) * mm});
            skCircle(sketch, "E94.0", {"center": v(-60, 67.5) * mm, "radius": 4 * mm});
            skCircle(sketch, "E95.0", {"center": v(60, 67.5) * mm, "radius": 4 * mm});
            skCircle(sketch, "E96.0", {"center": v(60, -67.5) * mm, "radius": 4 * mm});
            skCircle(sketch, "E97.0", {"center": v(-60, -67.5) * mm, "radius": 4 * mm});
            skLineSegment(sketch, "E98", {"start": v(0, 90) * mm, "end": v(0, 120) * mm});
            skPoint(sketch, "E98.endSnap0", {"position": v(0, 90) * mm});
            skCircle(sketch, "E99", {"center": v(0, 120) * mm, "radius": 6 * mm});
            skArc(sketch, "E100", {"start": v(-15, 120) * mm, "mid": v(0, 135) * mm, "end": v(15, 120) * mm});
            skLineSegment(sketch, "E101", {"start": v(-15, 120) * mm, "end": v(-15, 108) * mm});
            skLineSegment(sketch, "E102", {"start": v(15, 120) * mm, "end": v(15, 108) * mm});
            skLineSegment(sketch, "E103", {"start": v(-15, 108) * mm, "end": v(-33, 90) * mm});
            skLineSegment(sketch, "E104", {"start": v(15, 108) * mm, "end": v(33, 90) * mm});
            skLineSegment(sketch, "E105", {"start": v(-80, 0) * mm, "end": v(80, 0) * mm});
            skCircle(sketch, "E106.MirrorC", {"center": v(0, -120) * mm, "radius": 6 * mm});
            skLineSegment(sketch, "E107.MirrorCS", {"start": v(0, -90) * mm, "end": v(0, -120) * mm});
            skLineSegment(sketch, "E108.MirrorCS", {"start": v(15, -108) * mm, "end": v(33, -90) * mm});
            skLineSegment(sketch, "E109.MirrorCS", {"start": v(15, -120) * mm, "end": v(15, -108) * mm});
            skArc(sketch, "E110.MirrorCS", {"start": v(-15, -120) * mm, "mid": v(0, -135) * mm, "end": v(15, -120) * mm});
            skLineSegment(sketch, "E111.MirrorCS", {"start": v(-15, -120) * mm, "end": v(-15, -108) * mm});
            skLineSegment(sketch, "E112.MirrorCS", {"start": v(-15, -108) * mm, "end": v(-33, -90) * mm});
            skArc(sketch, "E113.0", {"start": v(-56.15, 48.18) * mm, "mid": v(-58.99, 44.68) * mm, "end": v(-60, 40.3) * mm});
            skSolve(sketch);
        }
        {
            var Q0;
            {var subQ2=sQuery(id+"F16.wireOp",EDGE,"E80.0");Q0=makeQuery(id+"F16.imprint","IMPRINT",FACE,{"disambiguationData":[TD([[makeQuery(id+"F16.imprint","IMPRINT",EDGE,{"derivedFrom":subQ2}),1.0]])]});}
            var Q1;
            {var subQ7=sQuery(id+"F16.wireOp",EDGE,"E82.0");Q1=makeQuery(id+"F16.imprint","IMPRINT",FACE,{"disambiguationData":[TD([[makeQuery(id+"F16.imprint","IMPRINT",EDGE,{"derivedFrom":subQ7}),1.0]])]});}
            var Q2;
            Q2=makeQuery(id+"F16.imprint","IMPRINT",FACE,{"disambiguationData":[TD([[makeQuery(id+"F16.imprint","IMPRINT",EDGE,{"derivedFrom":sQuery(id+"F16.wireOp",EDGE,"E106.MirrorC")}),1.0]])]});
            var Q3;
            Q3=makeQuery(id+"F16.imprint","IMPRINT",FACE,{"disambiguationData":[TD([[makeQuery(id+"F16.imprint","IMPRINT",EDGE,{"derivedFrom":sQuery(id+"F16.wireOp",EDGE,"E99")}),-1.0]])]});
            var Q4;
            Q4=makeQuery(id+"F2.opExtrude","CAP_FACE",FACE,{"disambiguationData":[OSD([sQuery(id+"F0.wireOp",EDGE,"E12"),sQuery(id+"F0.wireOp",EDGE,"E13"),sQuery(id+"F0.wireOp",EDGE,"E14"),sQuery(id+"F0.wireOp",EDGE,"E15"),sQuery(id+"F0.wireOp",EDGE,"E17.filletArc"),sQuery(id+"F0.wireOp",EDGE,"E18.filletArc"),sQuery(id+"F0.wireOp",EDGE,"E19.filletArc"),sQuery(id+"F0.wireOp",EDGE,"E20.filletArc"),sQuery(id+"F0.wireOp",EDGE,"E25.0"),sQuery(id+"F0.wireOp",EDGE,"E25.1"),sQuery(id+"F0.wireOp",EDGE,"E25.2"),sQuery(id+"F0.wireOp",EDGE,"E25.3"),sQuery(id+"F0.wireOp",EDGE,"E25.4"),sQuery(id+"F0.wireOp",EDGE,"E25.5"),sQuery(id+"F0.wireOp",EDGE,"E25.6"),sQuery(id+"F0.wireOp",EDGE,"E25.7")])],"isStart":false});
            extrude(context, id + "F17", {"entities" : qUnion([Q0, Q1, Q2, Q3]), "endBound" : BoundingType.UP_TO_SURFACE, "endBoundEntityFace" : qUnion([Q4]), "depth" : 25 * mm});
        }
    });
